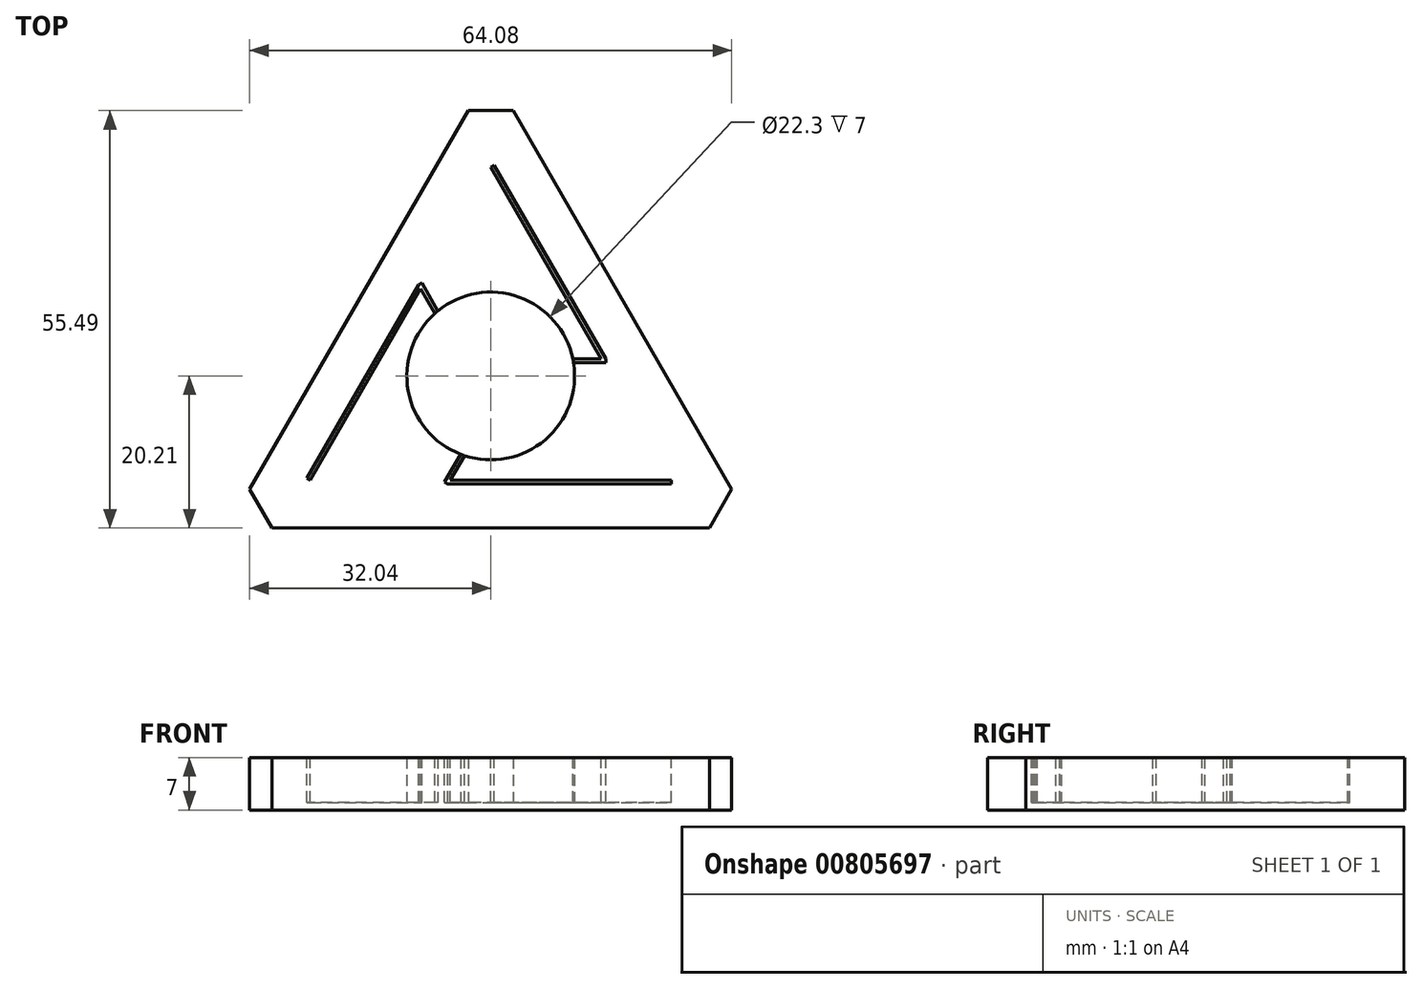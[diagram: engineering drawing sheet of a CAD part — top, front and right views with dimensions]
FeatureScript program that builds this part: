
annotation { "Feature Type Name" : "Feature", "Feature Type Description" : "" }
export const myFeature = defineFeature(function(context is Context, id is Id, definition is map)
    precondition{}
    {
        {
            var Q0;
            Q0=qCreatedBy(makeId("Top.planeOp"),FACE);
            var sketch = newSketch(context, id + "F0", { "sketchPlane" : qUnion([Q0])});
            skCircle(sketch, "E0.cCircle", {"center": v(0, 0) * mm, "radius": 20.2 * mm, "construction": true});
            skLineSegment(sketch, "E0.0", {"start": v(35, -20.2) * mm, "end": v(-35, -20.2) * mm});
            skLineSegment(sketch, "E0.1", {"start": v(-35, -20.2) * mm, "end": v(0, 40.41) * mm});
            skLineSegment(sketch, "E0.2", {"start": v(0, 40.41) * mm, "end": v(35, -20.2) * mm});
            skPoint(sketch, "E0.0.midPoint", {"position": v(0, -20.2) * mm});
            skCircle(sketch, "E1", {"center": v(0, 0) * mm, "radius": 11.15 * mm});
            skLineSegment(sketch, "E2", {"start": v(-2.96, 35.28) * mm, "end": v(2.96, 35.28) * mm});
            skLineSegment(sketch, "E3.1.0", {"start": v(-29.07, -20.2) * mm, "end": v(-32.04, -15.07) * mm});
            skLineSegment(sketch, "E3.2.0", {"start": v(32.04, -15.07) * mm, "end": v(29.07, -20.2) * mm});
            skSolve(sketch);
        }
        {
            var Q0;
            Q0=makeQuery(id+"F0.imprint","IMPRINT",FACE,{"disambiguationData":[TD([[makeQuery(id+"F0.imprint","IMPRINT",EDGE,{"derivedFrom":sQuery(id+"F0.wireOp",EDGE,"E1")}),-1.0]])]});
            extrude(context, id + "F1", {"entities" : qUnion([Q0]), "endBound" : BoundingType.SYMMETRIC, "depth" : 7 * mm, "offsetDistance" : 25 * mm});
        }
        {
            var Q0;
            Q0=makeQuery(id+"F1.opExtrude","CAP_FACE",FACE,{"disambiguationData":[OSD([sQuery(id+"F0.wireOp",EDGE,"E0.0"),sQuery(id+"F0.wireOp",EDGE,"E0.1"),sQuery(id+"F0.wireOp",EDGE,"E0.2"),sQuery(id+"F0.wireOp",EDGE,"E1"),sQuery(id+"F0.wireOp",EDGE,"E2"),sQuery(id+"F0.wireOp",EDGE,"E3.1.0"),sQuery(id+"F0.wireOp",EDGE,"E3.2.0")])],"isStart":false});
            var sketch = newSketch(context, id + "F2", { "sketchPlane" : qUnion([Q0])});
            skLineSegment(sketch, "E4.bottom", {"start": v(10.92, 2.25) * mm, "end": v(15.28, 2.25) * mm});
            skLineSegment(sketch, "E4.top", {"start": v(10.92, 1.75) * mm, "end": v(15.28, 1.75) * mm});
            skLineSegment(sketch, "E4.left", {"start": v(10.92, 2.25) * mm, "end": v(10.92, 1.75) * mm});
            skLineSegment(sketch, "E4.right", {"start": v(15.28, 2.25) * mm, "end": v(15.28, 1.75) * mm});
            skLineSegment(sketch, "E5", {"start": v(15.28, 2.25) * mm, "end": v(0.43, 27.97) * mm});
            skLineSegment(sketch, "E6", {"start": v(0.43, 27.97) * mm, "end": v(0, 27.72) * mm});
            skLineSegment(sketch, "E7", {"start": v(0, 27.72) * mm, "end": v(14.7, 2.25) * mm});
            skLineSegment(sketch, "E8.1.0", {"start": v(-9.6, 12.1) * mm, "end": v(-24.44, -13.61) * mm});
            skLineSegment(sketch, "E8.1.1", {"start": v(-6.98, 8.58) * mm, "end": v(-9.16, 12.36) * mm});
            skLineSegment(sketch, "E8.1.2", {"start": v(-7.41, 8.33) * mm, "end": v(-9.6, 12.1) * mm});
            skLineSegment(sketch, "E8.1.3", {"start": v(-24, -13.86) * mm, "end": v(-9.3, 11.6) * mm});
            skLineSegment(sketch, "E8.1.4", {"start": v(-7.41, 8.33) * mm, "end": v(-6.98, 8.58) * mm});
            skLineSegment(sketch, "E8.1.5", {"start": v(-24.44, -13.61) * mm, "end": v(-24, -13.86) * mm});
            skLineSegment(sketch, "E8.2.0", {"start": v(-5.69, -14.36) * mm, "end": v(24, -14.36) * mm});
            skLineSegment(sketch, "E8.2.1", {"start": v(-3.94, -10.33) * mm, "end": v(-6.12, -14.11) * mm});
            skLineSegment(sketch, "E8.2.2", {"start": v(-3.5, -10.58) * mm, "end": v(-5.69, -14.36) * mm});
            skLineSegment(sketch, "E8.2.3", {"start": v(24, -13.86) * mm, "end": v(-5.4, -13.86) * mm});
            skLineSegment(sketch, "E8.2.4", {"start": v(-3.5, -10.58) * mm, "end": v(-3.94, -10.33) * mm});
            skLineSegment(sketch, "E8.2.5", {"start": v(24, -14.36) * mm, "end": v(24, -13.86) * mm});
            skPoint(sketch, "E8.center", {"position": v(0, 0) * mm});
            skLineSegment(sketch, "E9", {"start": v(-9.6, 12.1) * mm, "end": v(-9.16, 12.36) * mm});
            skLineSegment(sketch, "E10", {"start": v(-6.12, -14.11) * mm, "end": v(-5.69, -14.36) * mm});
            skSolve(sketch);
        }
        {
            var Q0;
            Q0 = qSketchRegion(id + "F2", true);
            extrude(context, id + "F3", {"entities" : qUnion([Q0]), "operationType" : NewBodyOperationType.REMOVE, "oppositeDirection" : true, "depth" : 6 * mm, "offsetDistance" : 25 * mm});
        }
    });
